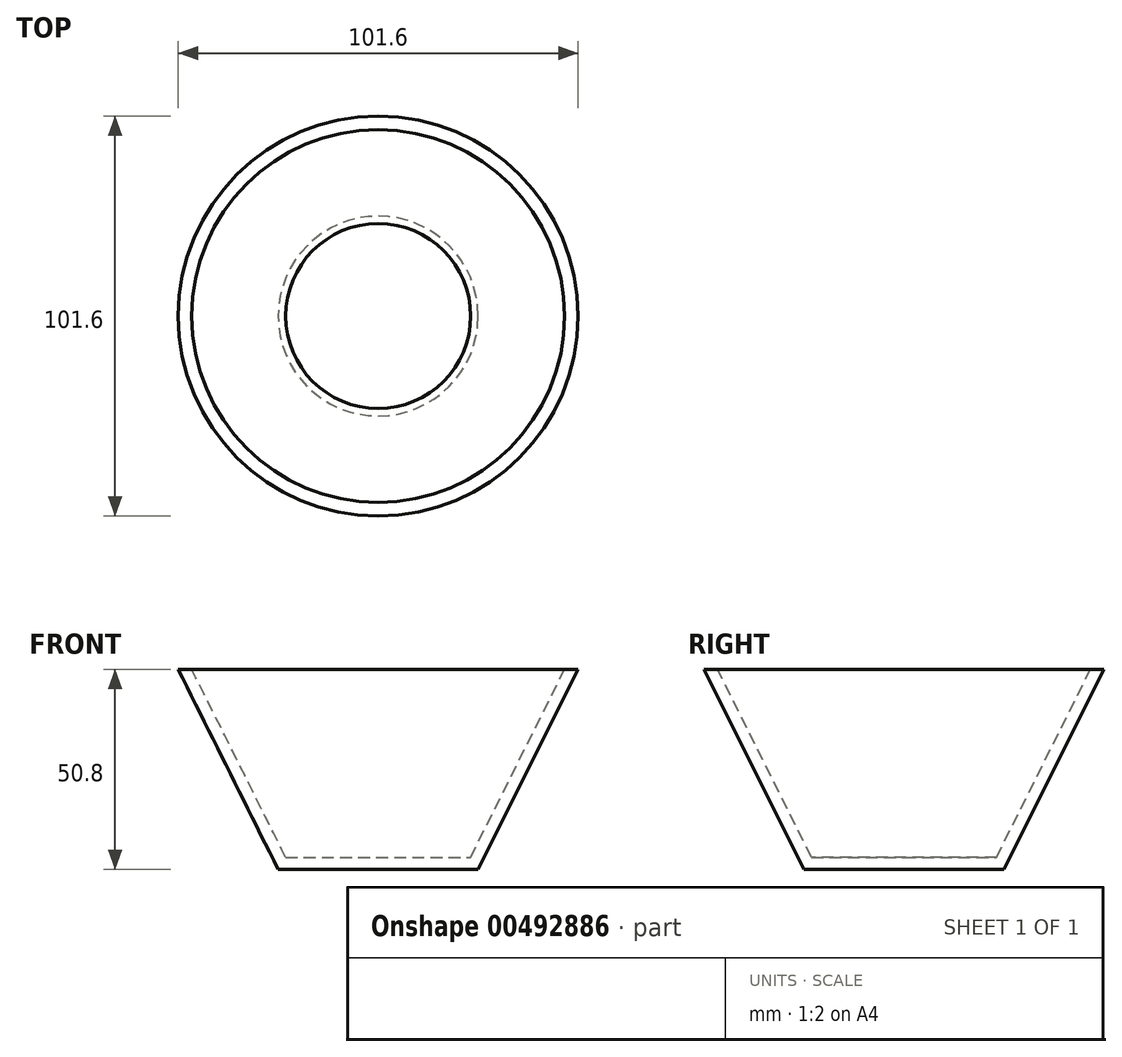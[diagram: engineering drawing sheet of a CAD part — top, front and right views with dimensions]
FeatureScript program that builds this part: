
annotation { "Feature Type Name" : "Feature", "Feature Type Description" : "" }
export const myFeature = defineFeature(function(context is Context, id is Id, definition is map)
    precondition{}
    {
        {
            var Q0;
            Q0=qCreatedBy(makeId("Front.planeOp"),FACE);
            var sketch = newSketch(context, id + "F0", { "sketchPlane" : qUnion([Q0])});
            skLineSegment(sketch, "E0", {"start": v(0, 0) * mm, "end": v(0, 50.8) * mm, "construction": true});
            skLineSegment(sketch, "E1", {"start": v(0, 0) * mm, "end": v(25.4, 0) * mm});
            skLineSegment(sketch, "E2", {"start": v(25.4, 0) * mm, "end": v(50.8, 50.8) * mm});
            skLineSegment(sketch, "E3.0", {"start": v(23.5, 3.07) * mm, "end": v(47.36, 50.8) * mm});
            skLineSegment(sketch, "E3.1", {"start": v(0, 3.07) * mm, "end": v(23.5, 3.07) * mm});
            skLineSegment(sketch, "E4", {"start": v(47.36, 50.8) * mm, "end": v(50.8, 50.8) * mm});
            skLineSegment(sketch, "E5", {"start": v(0, 3.07) * mm, "end": v(0, 0) * mm});
            skSolve(sketch);
        }
        {
            var Q0;
            Q0=makeQuery(id+"F0.imprint","IMPRINT",FACE,{"disambiguationData":[TD([[makeQuery(id+"F0.imprint","IMPRINT",EDGE,{"derivedFrom":sQuery(id+"F0.wireOp",EDGE,"E1")}),1.0]])]});
            var Q1;
            Q1=sQuery(id+"F0.wireOp",EDGE,"E0");
            revolve(context, id + "F1", {"entities" : qUnion([Q0]), "axis" : qUnion([Q1]), "revolveType" : RevolveType.FULL});
        }
    });
